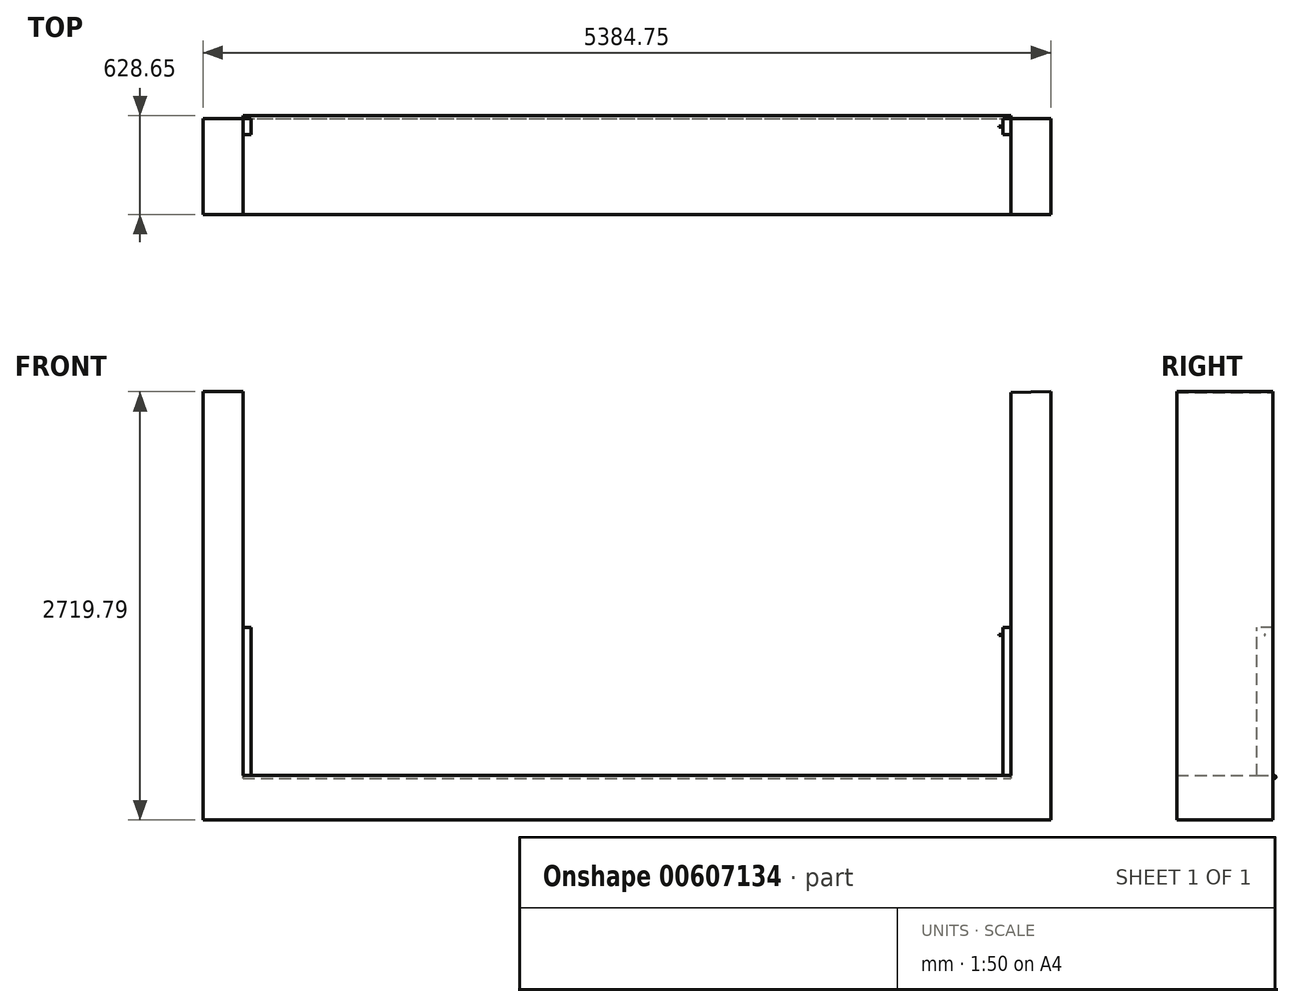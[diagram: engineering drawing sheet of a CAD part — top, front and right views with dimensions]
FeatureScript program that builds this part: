
annotation { "Feature Type Name" : "Feature", "Feature Type Description" : "" }
export const myFeature = defineFeature(function(context is Context, id is Id, definition is map)
    precondition{}
    {
        {
            var Q0;
            Q0=qCreatedBy(makeId("Front.planeOp"),FACE);
            var sketch = newSketch(context, id + "F0", { "sketchPlane" : qUnion([Q0])});
            skLineSegment(sketch, "E0", {"start": v(0, 0) * mm, "end": v(0, 2438.4) * mm});
            skLineSegment(sketch, "E1", {"start": v(0, 0) * mm, "end": v(4876.8, 0) * mm});
            skLineSegment(sketch, "E2", {"start": v(4876.8, 0) * mm, "end": v(4876.8, 2433.35) * mm});
            skLineSegment(sketch, "E3", {"start": v(0, 2438.4) * mm, "end": v(-254, 2438.4) * mm});
            skLineSegment(sketch, "E4", {"start": v(-254, 2438.4) * mm, "end": v(-254, -281.4) * mm});
            skLineSegment(sketch, "E5", {"start": v(-254, -281.4) * mm, "end": v(5130.75, -281.4) * mm});
            skLineSegment(sketch, "E6", {"start": v(5130.75, -281.4) * mm, "end": v(5130.75, 2438.4) * mm});
            skLineSegment(sketch, "E7", {"start": v(5130.75, 2438.4) * mm, "end": v(4876.8, 2433.35) * mm});
            skSolve(sketch);
        }
        {
            var Q0;
            Q0 = qSketchRegion(id + "F0", true);
            extrude(context, id + "F1", {"entities" : qUnion([Q0]), "depth" : 609.6 * mm, "offsetDistance" : 25.4 * mm});
        }
        {
            var Q0;
            Q0=makeQuery(id+"F1.opExtrude","SWEPT_FACE",FACE,{"disambiguationData":[OSD([sQuery(id+"F0.wireOp",EDGE,"E2")])]});
            var sketch = newSketch(context, id + "F2", { "sketchPlane" : qUnion([Q0])});
            skLineSegment(sketch, "E8", {"start": v(0, 0) * mm, "end": v(-12.7, 0) * mm});
            skLineSegment(sketch, "E9", {"start": v(-19.05, -6.35) * mm, "end": v(-19.05, -12.7) * mm});
            skLineSegment(sketch, "E10", {"start": v(-12.7, -19.05) * mm, "end": v(0, -19.05) * mm});
            skLineSegment(sketch, "E11", {"start": v(0, -19.05) * mm, "end": v(0, 0) * mm});
            skPoint(sketch, "E12.visualSharp", {"position": v(-19.05, 0) * mm});
            skArc(sketch, "E12.filletArc", {"start": v(-12.7, 0) * mm, "mid": v(-17.2, -1.86) * mm, "end": v(-19.05, -6.35) * mm});
            skPoint(sketch, "E13.visualSharp", {"position": v(-19.05, -19.05) * mm});
            skArc(sketch, "E13.filletArc", {"start": v(-19.05, -12.7) * mm, "mid": v(-17.2, -17.2) * mm, "end": v(-12.7, -19.05) * mm});
            skSolve(sketch);
        }
        {
            var Q0;
            Q0 = qSketchRegion(id + "F2", true);
            extrude(context, id + "F3", {"entities" : qUnion([Q0]), "operationType" : NewBodyOperationType.ADD, "depth" : 4876.8 * mm, "offsetDistance" : 25.4 * mm});
        }
        {
            var Q0;
            Q0=makeQuery(id+"F1.opExtrude","SWEPT_FACE",FACE,{"disambiguationData":[OSD([sQuery(id+"F0.wireOp",EDGE,"E0")])]});
            var sketch = newSketch(context, id + "F4", { "sketchPlane" : qUnion([Q0])});
            skLineSegment(sketch, "E14", {"start": v(0, 0) * mm, "end": v(-101.6, 0) * mm});
            skLineSegment(sketch, "E15", {"start": v(-101.6, 0) * mm, "end": v(-101.6, 939.8) * mm});
            skLineSegment(sketch, "E16", {"start": v(-101.6, 939.8) * mm, "end": v(0, 939.8) * mm});
            skLineSegment(sketch, "E17", {"start": v(0, 939.8) * mm, "end": v(0, 0) * mm});
            skSolve(sketch);
        }
        {
            var Q0;
            Q0 = qSketchRegion(id + "F4", true);
            extrude(context, id + "F5", {"entities" : qUnion([Q0]), "operationType" : NewBodyOperationType.ADD, "depth" : 50.8 * mm, "offsetDistance" : 25.4 * mm});
        }
        {
            var Q0;
            Q0=makeQuery(id+"F1.opExtrude","SWEPT_FACE",FACE,{"disambiguationData":[OSD([sQuery(id+"F0.wireOp",EDGE,"E2")])]});
            var sketch = newSketch(context, id + "F6", { "sketchPlane" : qUnion([Q0])});
            skLineSegment(sketch, "E18.bottom", {"start": v(0, 0) * mm, "end": v(101.6, 0) * mm});
            skLineSegment(sketch, "E18.top", {"start": v(0, 939.8) * mm, "end": v(101.6, 939.8) * mm});
            skLineSegment(sketch, "E18.left", {"start": v(0, 0) * mm, "end": v(0, 939.8) * mm});
            skLineSegment(sketch, "E18.right", {"start": v(101.6, 0) * mm, "end": v(101.6, 939.8) * mm});
            skSolve(sketch);
        }
        {
            var Q0;
            Q0 = qSketchRegion(id + "F6", true);
            extrude(context, id + "F7", {"entities" : qUnion([Q0]), "operationType" : NewBodyOperationType.ADD, "depth" : 50.8 * mm, "offsetDistance" : 25.4 * mm});
        }
        {
            var Q0;
            Q0=makeQuery(id+"F7.opExtrude","CAP_FACE",FACE,{"disambiguationData":[OSD([sQuery(id+"F6.wireOp",EDGE,"E18.bottom"),sQuery(id+"F6.wireOp",EDGE,"E18.top"),sQuery(id+"F6.wireOp",EDGE,"E18.left"),sQuery(id+"F6.wireOp",EDGE,"E18.right")])],"isStart":false});
            var sketch = newSketch(context, id + "F8", { "sketchPlane" : qUnion([Q0])});
            skCircle(sketch, "E19", {"center": v(50.8, 893.76) * mm, "radius": 3.18 * mm});
            skSolve(sketch);
        }
        {
            var Q0;
            Q0 = qSketchRegion(id + "F8", true);
            extrude(context, id + "F9", {"entities" : qUnion([Q0]), "operationType" : NewBodyOperationType.ADD, "depth" : 25.4 * mm, "offsetDistance" : 25.4 * mm});
        }
    });
